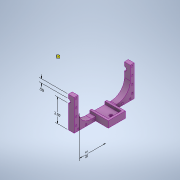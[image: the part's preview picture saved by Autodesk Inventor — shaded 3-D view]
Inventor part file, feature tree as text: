
AUTODESK INVENTOR PART (.ipt)
format: ipt  version: 2022 (Build 260153070, 153G)  size: 1,596,416 bytes
history: native  units: in
note: dims shown in document units (in); Inventor stores cm internally (conversion verified against a paired STEP export)
features: sketch x7, extrude x6, other x4, hole x2, mirror x2, fillet x1, split x1
ambient origin geometry x8: Origin, YZ Plane, XZ Plane, XY Plane, X Axis, Y Axis, Z Axis, Center Point
bodies: Solid1 (feature_tree)
feature tree (23):
  other  "Annotations"
  sketch  "Sketch1"  dims[d0=1.7in d1=4.25in]
  extrude  "Extrusion1"  Depth=4.25in
  extrude  "Extrusion2"  Depth=0.25in
  hole  "Hole1"  [1 undecoded]
  extrude  "Extrusion10"  TaperAngle=0.0deg  [1 undecoded]
  extrude  "Extrusion11"  Depth=0.5in
  extrude  "Extrusion12"  Depth=0.375in
  mirror  "Mirror8"
  fillet  "Fillet1"  Radius=0.375in
  extrude  "Extrusion13"  Depth=0.5in
  split  "Split1"
  hole  "Hole6"  [1 undecoded]
  mirror  "Mirror9"
  sketch  "Sketch2"  dims[d2=0.25in d3=0.25in]
  sketch  "Sketch15"  dims[d4=0.475in d5=0.0in]
  sketch  "Sketch16"  dims[d6=0.35in d7=0.0in]
  sketch  "Sketch17"  dims[d8=0.5in d9=0.5in]
  sketch  "Sketch18"  dims[d10=0.201in d11=0.75in d12=0.4in d13=0.1in d14=0.5635in d15=1.0in d16=0.8108in d17=0.375in d24=0.375in]
  sketch  "Sketch24"  dims[d101=2.75in d102=0.0in d103=0.5in d104=3.5in d105=0.0in d109=1.5in d115=0.0in d116=0.0in d117=1.75in d120=0.51in d140=0.05in d141=0.0in d149=3.225in d150=0.2375in d151=0.25in d152=0.25in d153=1.5748in d155=1.0in d156=0.3937in d158=1.0in d160=1.1811in d162=1.0in d163=0.3937in d165=1.0in d167=0.201in d168=0.75in d169=0.45in d170=0.15in d171=0.5635in d172=1.0in d173=0.8108in d106=0.9428in d107=4.2237in d108=3.35in d125=0.0966in d126=0.3041in d127=2.97in d128=0.1855in d129=0.2047in d130=0.495in d119=0.5in d121=0.5in d122=0.0344in]
  other  "Linear Dimension 4"
  other  "Linear Dimension 6"
  other  "Linear Dimension 7"
note: 3 required parameter values undecoded (feature->parameter linkage not recoverable at this tier; creation-order binding heuristic only, values carry confidence <= 0.55)
